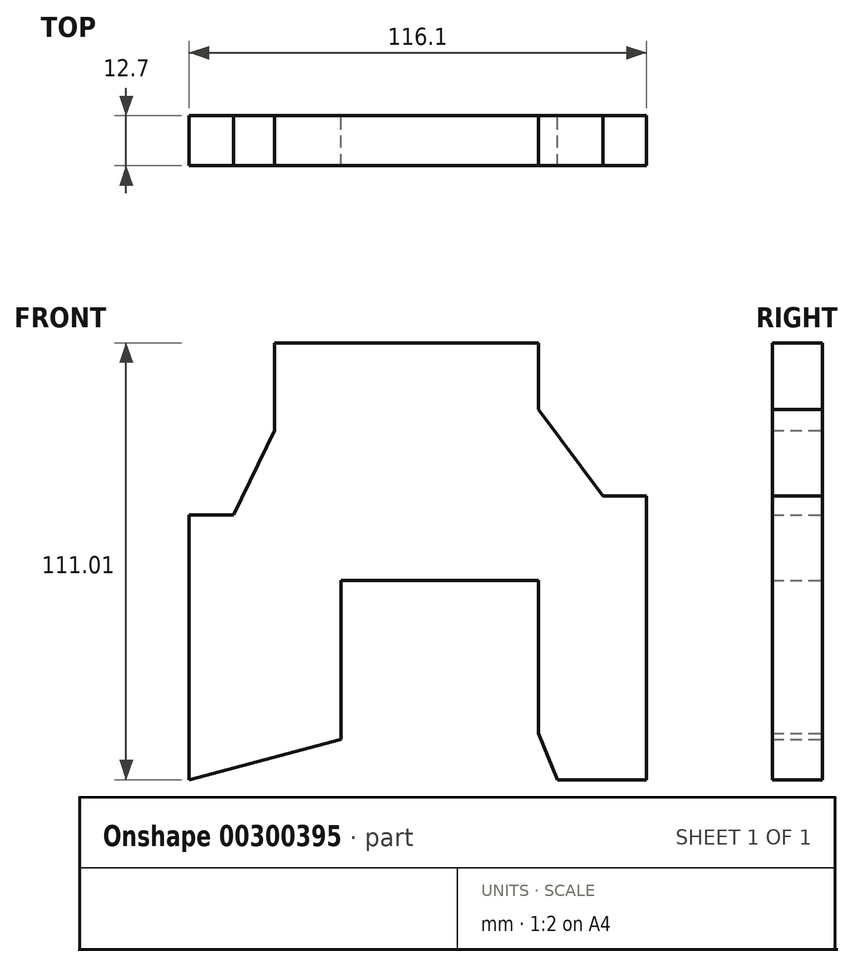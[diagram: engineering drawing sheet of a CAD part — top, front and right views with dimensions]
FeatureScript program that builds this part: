
annotation { "Feature Type Name" : "Feature", "Feature Type Description" : "" }
export const myFeature = defineFeature(function(context is Context, id is Id, definition is map)
    precondition{}
    {
        {
            var Q0;
            Q0=qCreatedBy(makeId("Front.planeOp"),FACE);
            var sketch = newSketch(context, id + "F0", { "sketchPlane" : qUnion([Q0])});
            skLineSegment(sketch, "E0", {"start": v(-34.57, 54.38) * mm, "end": v(32.46, 54.38) * mm});
            skLineSegment(sketch, "E1", {"start": v(32.46, 54.38) * mm, "end": v(32.46, 37.49) * mm});
            skLineSegment(sketch, "E2", {"start": v(32.46, 37.49) * mm, "end": v(48.82, 15.5) * mm});
            skLineSegment(sketch, "E3", {"start": v(48.82, 15.5) * mm, "end": v(59.81, 15.5) * mm});
            skLineSegment(sketch, "E4", {"start": v(59.81, 15.5) * mm, "end": v(59.81, -56.63) * mm});
            skLineSegment(sketch, "E5", {"start": v(59.81, -56.63) * mm, "end": v(37.29, -56.63) * mm});
            skLineSegment(sketch, "E6", {"start": v(37.29, -56.63) * mm, "end": v(32.46, -44.83) * mm});
            skLineSegment(sketch, "E7", {"start": v(32.46, -44.83) * mm, "end": v(32.46, -5.95) * mm});
            skLineSegment(sketch, "E8", {"start": v(32.46, -5.95) * mm, "end": v(-17.68, -5.95) * mm});
            skLineSegment(sketch, "E9", {"start": v(-17.68, -5.95) * mm, "end": v(-17.68, -46.44) * mm});
            skLineSegment(sketch, "E10", {"start": v(-17.68, -46.44) * mm, "end": v(-56.29, -56.63) * mm});
            skLineSegment(sketch, "E11", {"start": v(-56.29, -56.63) * mm, "end": v(-56.29, 10.67) * mm});
            skLineSegment(sketch, "E12", {"start": v(-56.29, 10.67) * mm, "end": v(-45.03, 10.67) * mm});
            skLineSegment(sketch, "E13", {"start": v(-45.03, 10.67) * mm, "end": v(-34.57, 32.12) * mm});
            skLineSegment(sketch, "E14", {"start": v(-34.57, 32.12) * mm, "end": v(-34.57, 54.38) * mm});
            skSolve(sketch);
        }
        {
            var Q0;
            Q0=makeQuery(id+"F0.imprint","IMPRINT",FACE,{"disambiguationData":[TD([[makeQuery(id+"F0.imprint","IMPRINT",EDGE,{"derivedFrom":sQuery(id+"F0.wireOp",EDGE,"E0")}),-1.0]])]});
            extrude(context, id + "F1", {"entities" : qUnion([Q0]), "depth" : 12.7 * mm});
        }
    });
